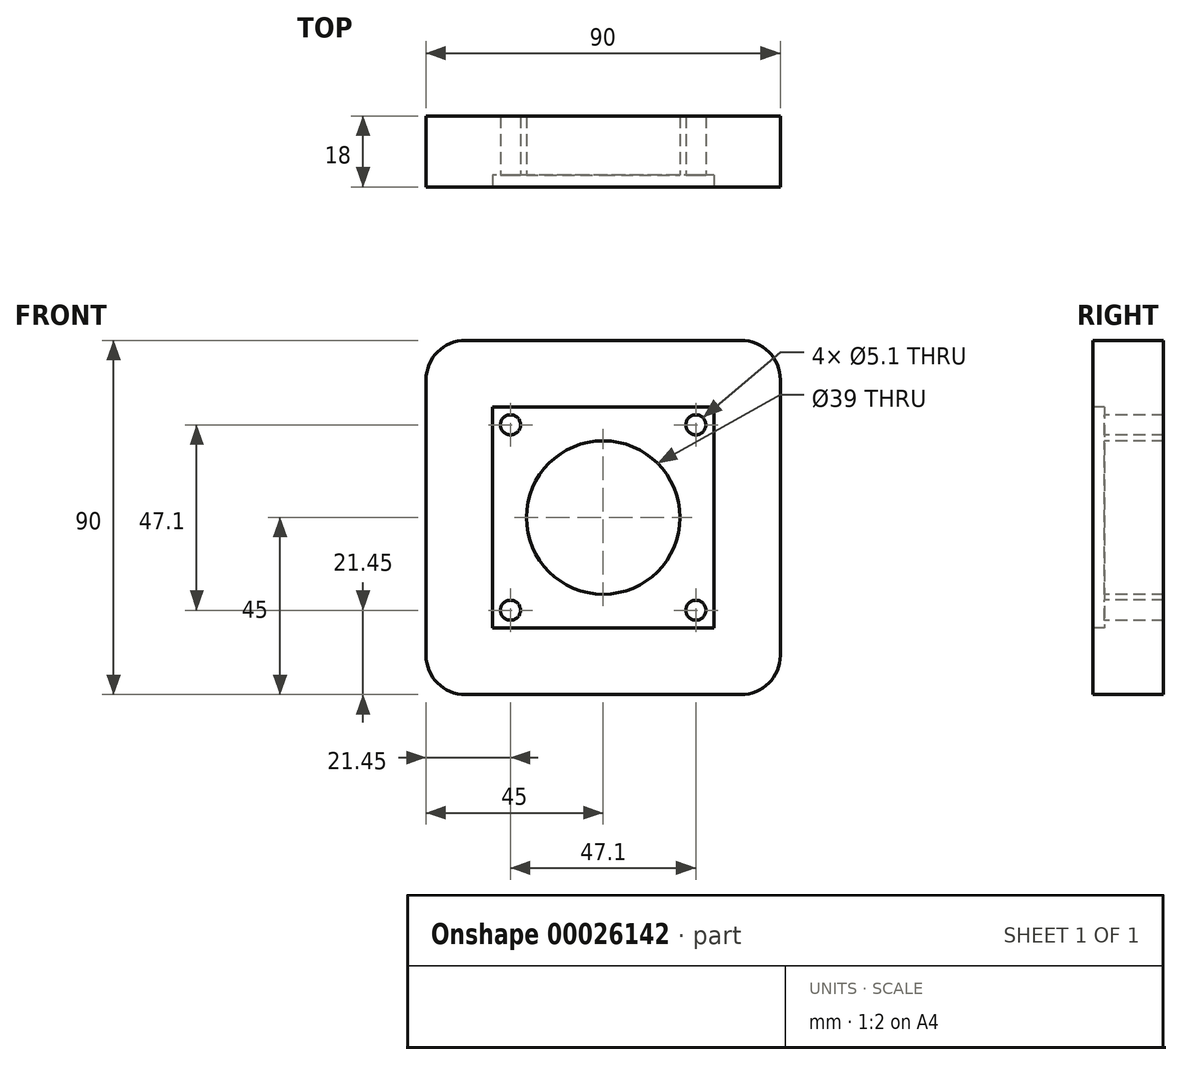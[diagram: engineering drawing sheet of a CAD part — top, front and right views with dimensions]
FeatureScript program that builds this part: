
annotation { "Feature Type Name" : "Feature", "Feature Type Description" : "" }
export const myFeature = defineFeature(function(context is Context, id is Id, definition is map)
    precondition{}
    {
        {
            var Q0;
            Q0=qCreatedBy(makeId("Front.planeOp"),FACE);
            var sketch = newSketch(context, id + "F0", { "sketchPlane" : qUnion([Q0])});
            skLineSegment(sketch, "E0.rect.bottom", {"start": v(35, -45) * mm, "end": v(-35, -45) * mm});
            skLineSegment(sketch, "E0.rect.top", {"start": v(35, 45) * mm, "end": v(-35, 45) * mm});
            skLineSegment(sketch, "E0.rect.left", {"start": v(45, -35) * mm, "end": v(45, 35) * mm});
            skLineSegment(sketch, "E0.rect.right", {"start": v(-45, -35) * mm, "end": v(-45, 35) * mm});
            skPoint(sketch, "E0.rect.middle", {"position": v(0, 0) * mm});
            skLineSegment(sketch, "E1.rect.bottom", {"start": v(28.1, 28.1) * mm, "end": v(-28.1, 28.1) * mm});
            skLineSegment(sketch, "E1.rect.top", {"start": v(28.1, -28.1) * mm, "end": v(-28.1, -28.1) * mm});
            skLineSegment(sketch, "E1.rect.left", {"start": v(28.1, 28.1) * mm, "end": v(28.1, -28.1) * mm});
            skLineSegment(sketch, "E1.rect.right", {"start": v(-28.1, 28.1) * mm, "end": v(-28.1, -28.1) * mm});
            skPoint(sketch, "E2.visualSharp", {"position": v(-45, 45) * mm});
            skArc(sketch, "E2.filletArc", {"start": v(-35, 45) * mm, "mid": v(-42.07, 42.07) * mm, "end": v(-45, 35) * mm});
            skPoint(sketch, "E3.visualSharp", {"position": v(45, 45) * mm});
            skArc(sketch, "E3.filletArc", {"start": v(45, 35) * mm, "mid": v(42.07, 42.07) * mm, "end": v(35, 45) * mm});
            skPoint(sketch, "E4.visualSharp", {"position": v(45, -45) * mm});
            skArc(sketch, "E4.filletArc", {"start": v(35, -45) * mm, "mid": v(42.07, -42.07) * mm, "end": v(45, -35) * mm});
            skPoint(sketch, "E5.visualSharp", {"position": v(-45, -45) * mm});
            skArc(sketch, "E5.filletArc", {"start": v(-45, -35) * mm, "mid": v(-42.07, -42.07) * mm, "end": v(-35, -45) * mm});
            skLineSegment(sketch, "E6.rect.bottom", {"start": v(23.55, 23.55) * mm, "end": v(-23.55, 23.55) * mm, "construction": true});
            skLineSegment(sketch, "E6.rect.top", {"start": v(23.55, -23.55) * mm, "end": v(-23.55, -23.55) * mm, "construction": true});
            skLineSegment(sketch, "E6.rect.left", {"start": v(23.55, 23.55) * mm, "end": v(23.55, -23.55) * mm, "construction": true});
            skLineSegment(sketch, "E6.rect.right", {"start": v(-23.55, 23.55) * mm, "end": v(-23.55, -23.55) * mm, "construction": true});
            skCircle(sketch, "E7", {"center": v(-23.55, 23.55) * mm, "radius": 2.55 * mm});
            skCircle(sketch, "E8", {"center": v(23.55, 23.55) * mm, "radius": 2.55 * mm});
            skCircle(sketch, "E9", {"center": v(23.55, -23.55) * mm, "radius": 2.55 * mm});
            skCircle(sketch, "E10", {"center": v(-23.55, -23.55) * mm, "radius": 2.55 * mm});
            skCircle(sketch, "E11", {"center": v(0, 0) * mm, "radius": 19.5 * mm});
            skSolve(sketch);
        }
        {
            var Q0;
            Q0 = qSketchRegion(id + "F0", true);
            var Q1;
            Q1=makeQuery(id+"F0.imprint","IMPRINT",FACE,{"disambiguationData":[TD([[makeQuery(id+"F0.imprint","IMPRINT",EDGE,{"derivedFrom":sQuery(id+"F0.wireOp",EDGE,"E1.rect.bottom")}),1.0]])]});
            extrude(context, id + "F1", {"entities" : qUnion([Q0, Q1]), "oppositeDirection" : true, "depth" : 18 * mm});
        }
        {
            var Q0;
            Q0=makeQuery(id+"F0.imprint","IMPRINT",FACE,{"disambiguationData":[TD([[makeQuery(id+"F0.imprint","IMPRINT",EDGE,{"derivedFrom":sQuery(id+"F0.wireOp",EDGE,"E1.rect.bottom")}),1.0]])]});
            extrude(context, id + "F2", {"entities" : qUnion([Q0]), "operationType" : NewBodyOperationType.REMOVE, "oppositeDirection" : true, "depth" : 3 * mm});
        }
    });
